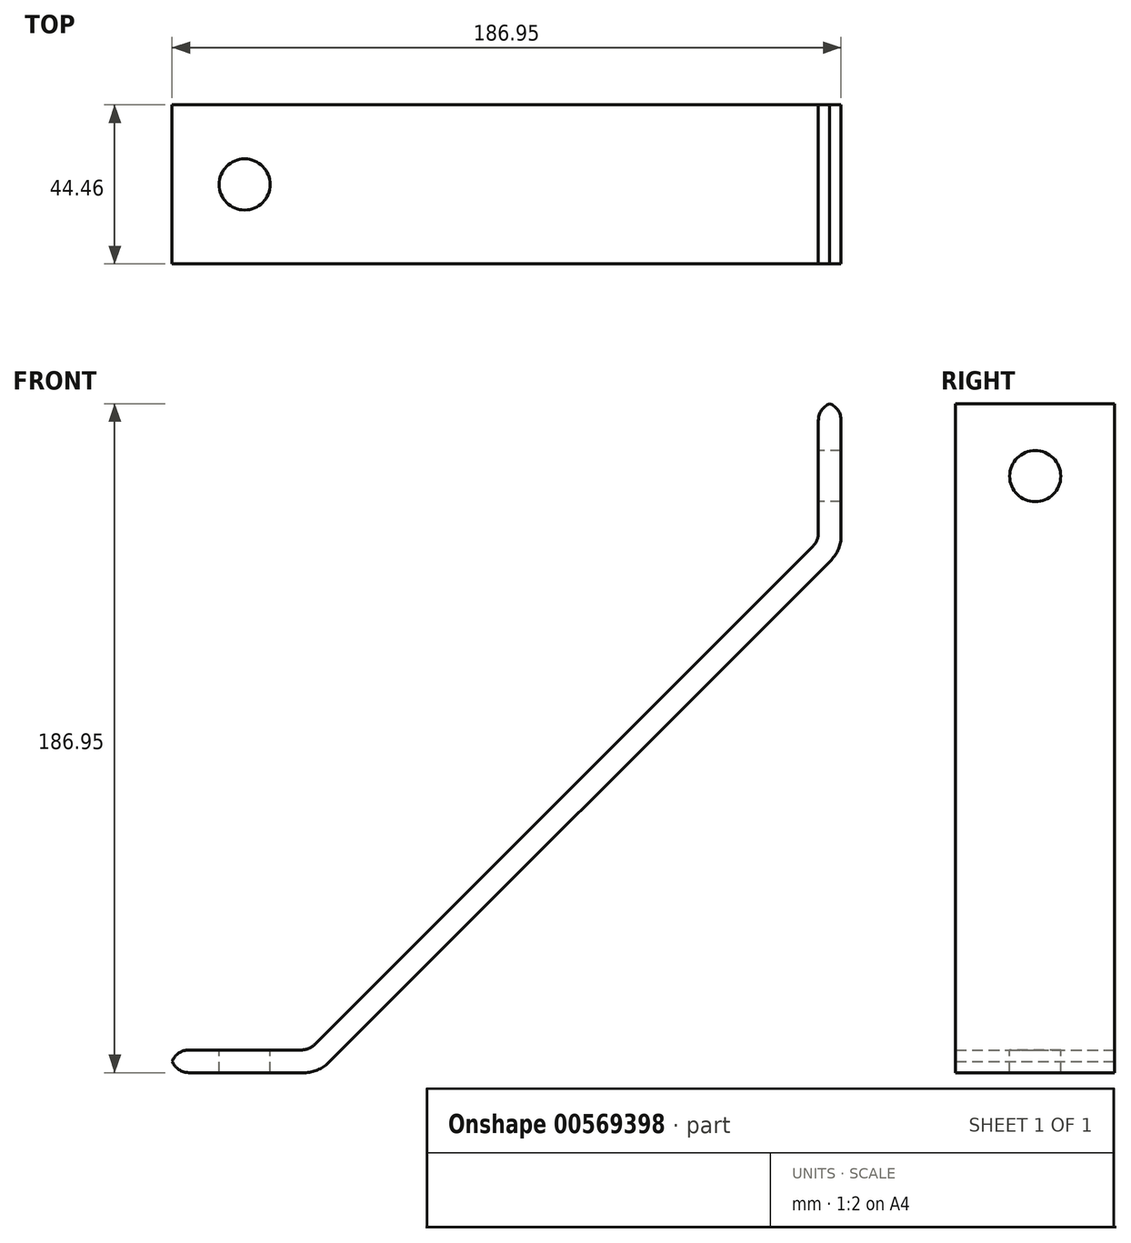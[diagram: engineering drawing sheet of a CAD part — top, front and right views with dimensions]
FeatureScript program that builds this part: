
annotation { "Feature Type Name" : "Feature", "Feature Type Description" : "" }
export const myFeature = defineFeature(function(context is Context, id is Id, definition is map)
    precondition{}
    {
        {
            var Q0;
            Q0=qCreatedBy(makeId("Front.planeOp"),FACE);
            var sketch = newSketch(context, id + "F0", { "sketchPlane" : qUnion([Q0])});
            skLineSegment(sketch, "E0", {"start": v(-76.24, 0) * mm, "end": v(-37.33, 0) * mm});
            skLineSegment(sketch, "E1", {"start": v(108.72, 146.05) * mm, "end": v(108.72, 184.96) * mm});
            skLineSegment(sketch, "E2.0", {"start": v(-76.24, 6.35) * mm, "end": v(-39.96, 6.35) * mm});
            skLineSegment(sketch, "E3.0", {"start": v(102.37, 148.68) * mm, "end": v(102.37, 184.96) * mm});
            skLineSegment(sketch, "E4", {"start": v(102.37, 184.96) * mm, "end": v(102.37, 187.32) * mm});
            skLineSegment(sketch, "E5", {"start": v(102.37, 187.32) * mm, "end": v(108.72, 187.32) * mm});
            skLineSegment(sketch, "E6", {"start": v(108.72, 187.32) * mm, "end": v(108.72, 184.96) * mm});
            skLineSegment(sketch, "E7", {"start": v(-76.24, 0) * mm, "end": v(-78.6, 0) * mm});
            skLineSegment(sketch, "E8", {"start": v(-78.6, 0) * mm, "end": v(-78.6, 6.35) * mm});
            skLineSegment(sketch, "E9", {"start": v(-78.6, 6.35) * mm, "end": v(-76.24, 6.35) * mm});
            skLineSegment(sketch, "E10", {"start": v(-78.6, 0) * mm, "end": v(-37.33, 0) * mm});
            skLineSegment(sketch, "E11", {"start": v(108.72, 187.32) * mm, "end": v(108.72, 146.05) * mm});
            skLineSegment(sketch, "E12", {"start": v(108.72, 146.05) * mm, "end": v(-37.33, 0) * mm});
            skLineSegment(sketch, "E13.0", {"start": v(102.37, 148.68) * mm, "end": v(-39.96, 6.35) * mm});
            skSolve(sketch);
        }
        {
            var Q0;
            Q0 = qSketchRegion(id + "F0", true);
            extrude(context, id + "F1", {"entities" : qUnion([Q0]), "endBound" : BoundingType.SYMMETRIC, "depth" : 44.45 * mm, "offsetDistance" : 25.4 * mm});
        }
        {
            var Q0;
            Q0=makeQuery(id+"F1.opExtrude","SWEPT_EDGE",EDGE,{"disambiguationData":[OSD([sQuery(id+"F0.wireOp",EDGE,"E2.0"),sQuery(id+"F0.wireOp",EDGE,"E13.0")])]});
            var Q1;
            Q1=makeQuery(id+"F1.opExtrude","SWEPT_EDGE",EDGE,{"disambiguationData":[OSD([sQuery(id+"F0.wireOp",EDGE,"E3.0"),sQuery(id+"F0.wireOp",EDGE,"E13.0")])]});
            fillet(context, id + "F2", {"entities" : qUnion([Q0, Q1]), "radius" : 5.08 * mm, "tangentPropagation" : true, "allowEdgeOverflow" : false});
        }
        {
            var Q0;
            Q0=makeQuery(id+"F1.opExtrude","SWEPT_EDGE",EDGE,{"disambiguationData":[OSD([sQuery(id+"F0.wireOp",EDGE,"E11"),sQuery(id+"F0.wireOp",EDGE,"E12")])]});
            var Q1;
            Q1=makeQuery(id+"F1.opExtrude","SWEPT_EDGE",EDGE,{"disambiguationData":[OSD([sQuery(id+"F0.wireOp",EDGE,"E10"),sQuery(id+"F0.wireOp",EDGE,"E12")])]});
            fillet(context, id + "F3", {"entities" : qUnion([Q0, Q1]), "radius" : 9.52 * mm, "tangentPropagation" : true, "allowEdgeOverflow" : false});
        }
        {
            var Q0;
            Q0=makeQuery(id+"F1.opExtrude","SWEPT_FACE",FACE,{"disambiguationData":[OSD([sQuery(id+"F0.wireOp",EDGE,"E2.0"),sQuery(id+"F0.wireOp",EDGE,"E9")])]});
            var sketch = newSketch(context, id + "F4", { "sketchPlane" : qUnion([Q0])});
            skCircle(sketch, "E14", {"center": v(-57.96, 0) * mm, "radius": 7.14 * mm});
            skSolve(sketch);
        }
        {
            var Q0;
            Q0 = qSketchRegion(id + "F4", true);
            extrude(context, id + "F5", {"entities" : qUnion([Q0]), "operationType" : NewBodyOperationType.REMOVE, "oppositeDirection" : true, "depth" : 25.4 * mm, "offsetDistance" : 25.4 * mm});
        }
        {
            var Q0;
            Q0=makeQuery(id+"F1.opExtrude","SWEPT_FACE",FACE,{"disambiguationData":[OSD([sQuery(id+"F0.wireOp",EDGE,"E3.0"),sQuery(id+"F0.wireOp",EDGE,"E4")])]});
            var sketch = newSketch(context, id + "F6", { "sketchPlane" : qUnion([Q0])});
            skCircle(sketch, "E15", {"center": v(0, 166.67) * mm, "radius": 7.14 * mm});
            skSolve(sketch);
        }
        {
            var Q0;
            Q0 = qSketchRegion(id + "F6", true);
            extrude(context, id + "F7", {"entities" : qUnion([Q0]), "operationType" : NewBodyOperationType.REMOVE, "oppositeDirection" : true, "depth" : 25.4 * mm, "offsetDistance" : 25.4 * mm});
        }
        {
            var Q0;
            Q0=makeQuery(id+"F1.opExtrude","SWEPT_EDGE",EDGE,{"disambiguationData":[OSD([sQuery(id+"F0.wireOp",EDGE,"E5"),sQuery(id+"F0.wireOp",EDGE,"E11")])]});
            var Q1;
            Q1=makeQuery(id+"F1.opExtrude","SWEPT_EDGE",EDGE,{"disambiguationData":[OSD([sQuery(id+"F0.wireOp",EDGE,"E8"),sQuery(id+"F0.wireOp",EDGE,"E10")])]});
            fillet(context, id + "F8", {"entities" : qUnion([Q0, Q1]), "radius" : 5.08 * mm, "tangentPropagation" : true, "allowEdgeOverflow" : false});
        }
    });
